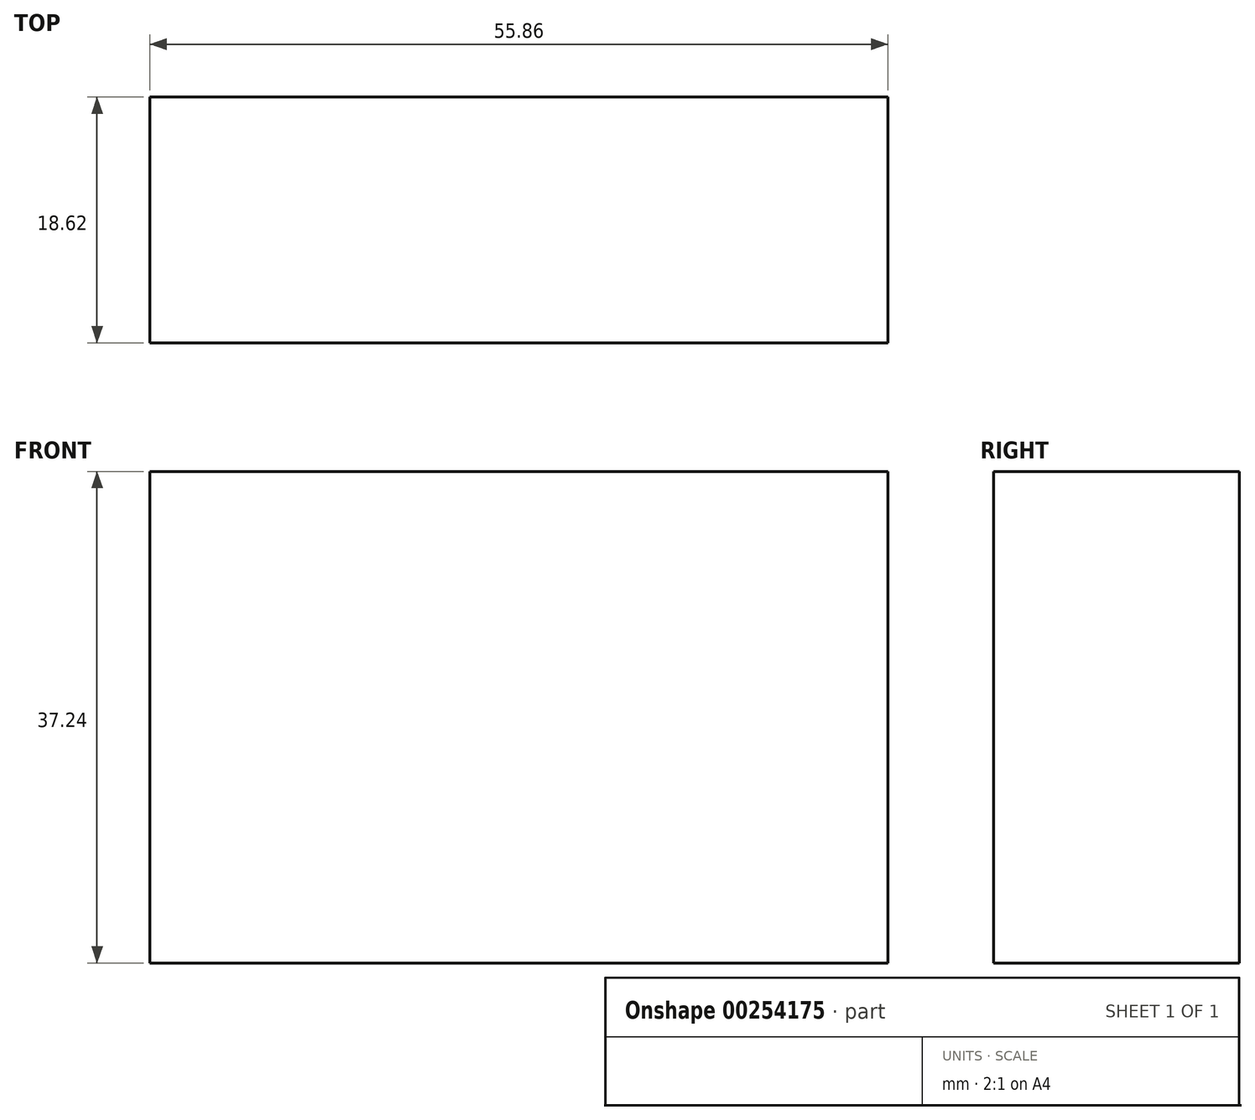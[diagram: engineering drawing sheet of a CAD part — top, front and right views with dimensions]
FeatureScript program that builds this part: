
annotation { "Feature Type Name" : "Feature", "Feature Type Description" : "" }
export const myFeature = defineFeature(function(context is Context, id is Id, definition is map)
    precondition{}
    {
        {
            var Q0;
            Q0=qCreatedBy(makeId("Front.planeOp"),FACE);
            var sketch = newSketch(context, id + "F0", { "sketchPlane" : qUnion([Q0])});
            skLineSegment(sketch, "E0.bottom", {"start": v(-33.45, -8.95) * mm, "end": v(-14.83, -8.95) * mm});
            skLineSegment(sketch, "E0.top", {"start": v(-33.45, 9.67) * mm, "end": v(-14.83, 9.67) * mm});
            skLineSegment(sketch, "E0.left", {"start": v(-33.45, -8.95) * mm, "end": v(-33.45, 9.67) * mm});
            skLineSegment(sketch, "E0.right", {"start": v(-14.83, -8.95) * mm, "end": v(-14.83, 9.67) * mm});
            skLineSegment(sketch, "E1.MirrorCS", {"start": v(3.79, 9.67) * mm, "end": v(-14.83, 9.67) * mm});
            skLineSegment(sketch, "E2.MirrorCS", {"start": v(3.79, -8.95) * mm, "end": v(3.79, 9.67) * mm});
            skLineSegment(sketch, "E3.MirrorCS", {"start": v(3.79, -8.95) * mm, "end": v(-14.83, -8.95) * mm});
            skLineSegment(sketch, "E4.MirrorCS", {"start": v(3.79, 9.67) * mm, "end": v(22.4, 9.67) * mm});
            skLineSegment(sketch, "E5.MirrorCS", {"start": v(22.4, -8.95) * mm, "end": v(22.4, 9.67) * mm});
            skLineSegment(sketch, "E6.MirrorCS", {"start": v(3.79, -8.95) * mm, "end": v(22.4, -8.95) * mm});
            skLineSegment(sketch, "E7.MirrorCS", {"start": v(-33.45, 28.29) * mm, "end": v(-33.45, 9.67) * mm});
            skLineSegment(sketch, "E8.MirrorCS", {"start": v(-14.83, 28.29) * mm, "end": v(-14.83, 9.67) * mm});
            skLineSegment(sketch, "E9.MirrorCS", {"start": v(-33.45, 28.29) * mm, "end": v(-14.83, 28.29) * mm});
            skLineSegment(sketch, "E10.MirrorCS", {"start": v(3.79, 28.29) * mm, "end": v(-14.83, 28.29) * mm});
            skLineSegment(sketch, "E11.MirrorCS", {"start": v(3.79, 28.29) * mm, "end": v(3.79, 9.67) * mm});
            skLineSegment(sketch, "E12.MirrorCS", {"start": v(22.4, 28.29) * mm, "end": v(22.4, 9.67) * mm});
            skLineSegment(sketch, "E13.MirrorCS", {"start": v(3.79, 28.29) * mm, "end": v(22.4, 28.29) * mm});
            skSolve(sketch);
        }
        {
            var Q0;
            Q0 = qSketchRegion(id + "F0", true);
            extrude(context, id + "F1", {"entities" : qUnion([Q0]), "depth" : 18.62 * mm});
        }
    });
